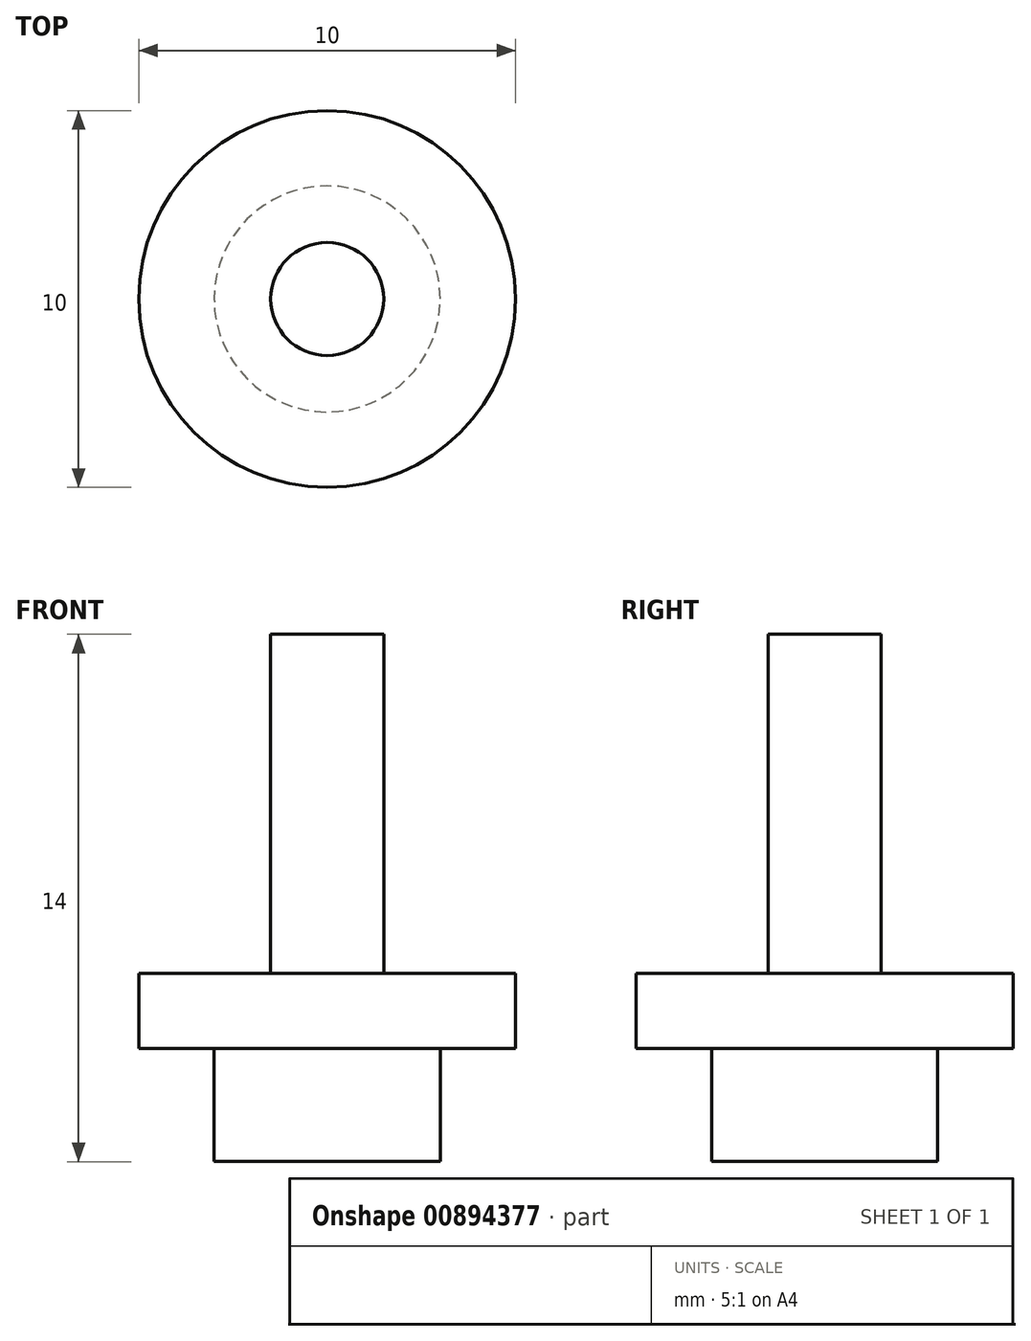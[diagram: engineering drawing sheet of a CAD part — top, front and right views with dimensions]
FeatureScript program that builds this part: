
annotation { "Feature Type Name" : "Feature", "Feature Type Description" : "" }
export const myFeature = defineFeature(function(context is Context, id is Id, definition is map)
    precondition{}
    {
        {
            var Q0;
            Q0=qCreatedBy(makeId("Right.planeOp"),FACE);
            var sketch = newSketch(context, id + "F0", { "sketchPlane" : qUnion([Q0])});
            skLineSegment(sketch, "E0.bottom", {"start": v(3, -2.12) * mm, "end": v(-2, -2.12) * mm});
            skLineSegment(sketch, "E0.top", {"start": v(3, -4.12) * mm, "end": v(-2, -4.12) * mm});
            skLineSegment(sketch, "E0.left", {"start": v(3, -2.12) * mm, "end": v(3, -4.12) * mm});
            skLineSegment(sketch, "E0.right", {"start": v(-2, -2.12) * mm, "end": v(-2, -4.12) * mm});
            skLineSegment(sketch, "E1.bottom", {"start": v(3, -2.12) * mm, "end": v(1.5, -2.12) * mm});
            skLineSegment(sketch, "E1.top", {"start": v(3, 6.88) * mm, "end": v(1.5, 6.88) * mm});
            skLineSegment(sketch, "E1.left", {"start": v(3, -2.12) * mm, "end": v(3, 6.88) * mm});
            skLineSegment(sketch, "E1.right", {"start": v(1.5, -2.12) * mm, "end": v(1.5, 6.88) * mm});
            skLineSegment(sketch, "E2.bottom", {"start": v(3, -4.12) * mm, "end": v(0, -4.12) * mm});
            skLineSegment(sketch, "E2.top", {"start": v(3, -7.12) * mm, "end": v(0, -7.12) * mm});
            skLineSegment(sketch, "E2.left", {"start": v(3, -4.12) * mm, "end": v(3, -7.12) * mm});
            skLineSegment(sketch, "E2.right", {"start": v(0, -4.12) * mm, "end": v(0, -7.12) * mm});
            skSolve(sketch);
        }
        {
            var Q0;
            Q0 = qSketchRegion(id + "F0", true);
            var Q1;
            Q1=sQuery(id+"F0.wireOp",EDGE,"E1.left");
            revolve(context, id + "F1", {"surfaceOperationType" : NewSurfaceOperationType.NEW, "entities" : qUnion([Q0]), "axis" : qUnion([Q1]), "revolveType" : RevolveType.FULL});
        }
    });
